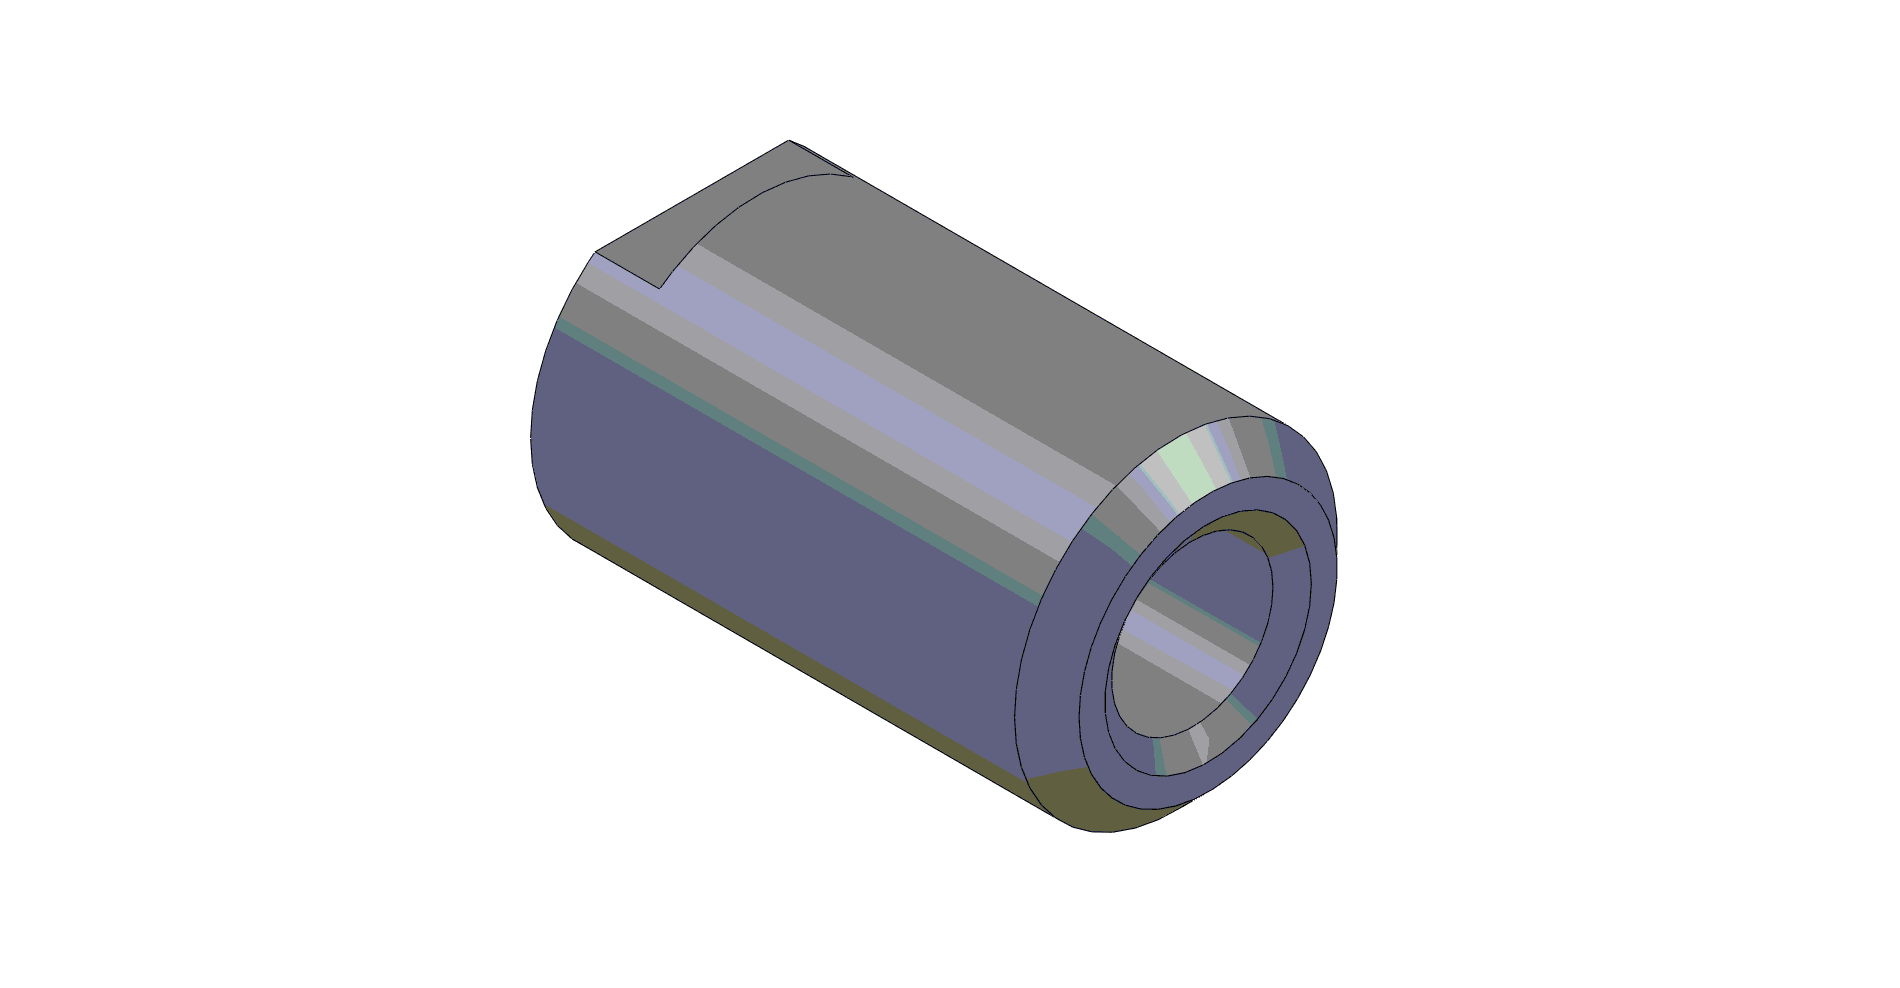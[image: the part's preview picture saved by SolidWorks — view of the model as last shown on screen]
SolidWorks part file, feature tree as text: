
SOLIDWORKS PART (.sldprt)
format: sldprt  version: not decoded by parser v0  size: 215,552 bytes
history: native  units: mm
features: sketch x4, plane x3, thread x2, material x1, revolve x1, hole x1, chamfer x1, cut_extrude x1 (+13 scaffold rows collapsed)
feature tree (27):
  scaffold x13  (default folders/planes/origin — collapsed)
  material  "Материал <не указан>"
  plane  "Спереди"
  plane  "Сверху"
  plane  "Справа"
  sketch  "Эскиз1"  dims[D1=2.5mm D2=5.0mm D3=8.0mm]
  revolve  "Повернуть1"  [1 undecoded]
  thread  "Отверстие резьбы1"  Diameter=3mm  [1 undecoded]
  thread  "Условное изображение резьбы1"  Diameter=5mm  [1 undecoded]
  hole  "Отверстие обработанное метчиком M31"  [1 undecoded]
  sketch  "Эскиз3"
  sketch  "Эскиз2"  dims[hole-wizard template sketch: 47 standard entries collapsed; hole parameters kept: c15.Глубина проходного сверла=8.0mm c15.Диаметр передней зенковки=3.2mm c15.D4=~3.666174mm c15.Угол передней зенковки=110.0deg c15.Диаметр задней зенковки=3.2mm c15.D6=~9.919017mm c15.Угол задней зенковки=110.0deg]
  chamfer  "Фаска1"  Distance=0.5mm Angle=45deg
  sketch  "Эскиз4"  dims[D1=4.0mm]
  cut_extrude  "Вырез-Вытянуть1"  Depth=1mm
decode coverage: 7 of 10 modeling features carry decoded parameters
note: ~ marks probable driven/reference dimensions
note: 4 parameter values undecoded
note: suppression state not decoded; provenance and decode notes live in map.json
